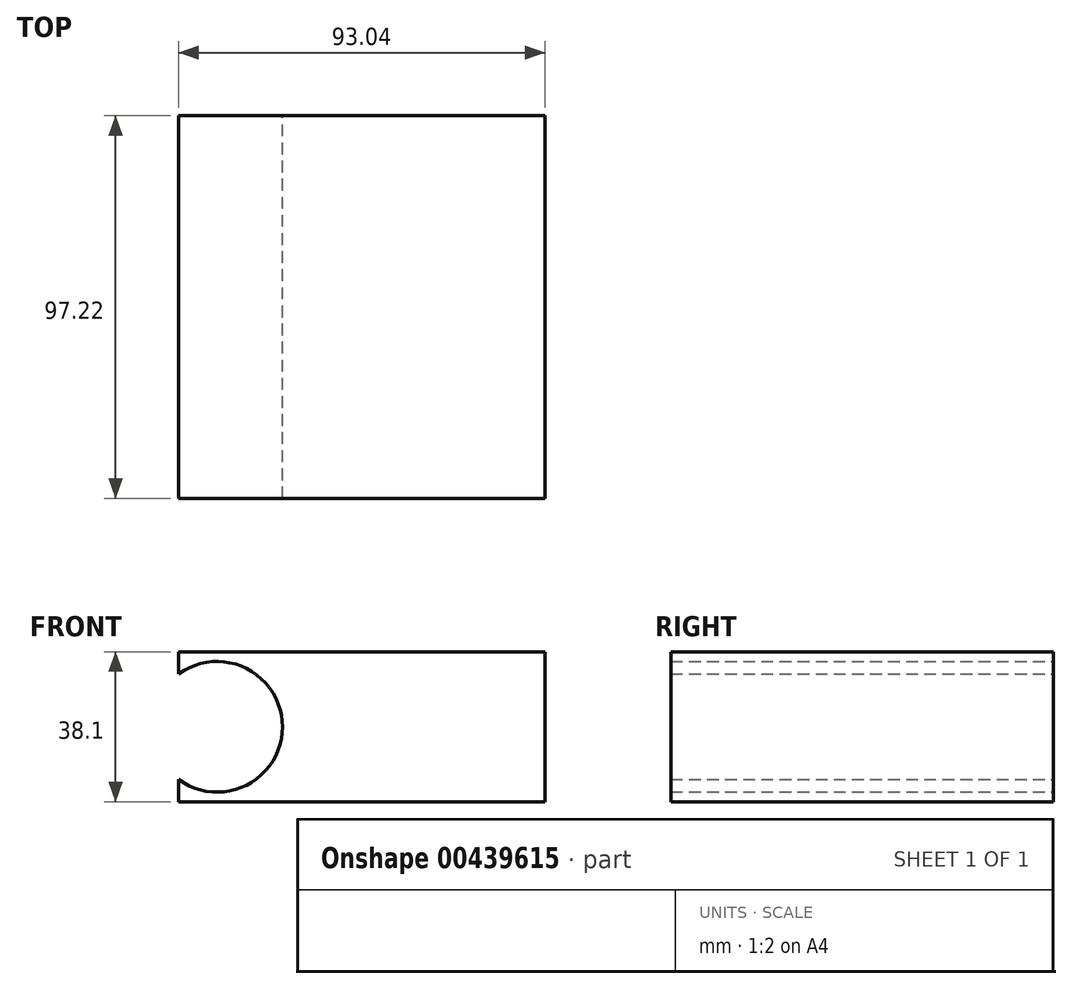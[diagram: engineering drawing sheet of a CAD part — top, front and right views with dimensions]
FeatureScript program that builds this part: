
annotation { "Feature Type Name" : "Feature", "Feature Type Description" : "" }
export const myFeature = defineFeature(function(context is Context, id is Id, definition is map)
    precondition{}
    {
        {
            var Q0;
            Q0=qCreatedBy(makeId("Top.planeOp"),FACE);
            var sketch = newSketch(context, id + "F0", { "sketchPlane" : qUnion([Q0])});
            skLineSegment(sketch, "E0.bottom", {"start": v(46.52, 48.61) * mm, "end": v(-46.52, 48.61) * mm});
            skLineSegment(sketch, "E0.top", {"start": v(46.52, -48.61) * mm, "end": v(-46.52, -48.61) * mm});
            skLineSegment(sketch, "E0.left", {"start": v(46.52, 48.61) * mm, "end": v(46.52, -48.61) * mm});
            skLineSegment(sketch, "E0.right", {"start": v(-46.52, 48.61) * mm, "end": v(-46.52, -48.61) * mm});
            skPoint(sketch, "E0.middle", {"position": v(0, 0) * mm});
            skSolve(sketch);
        }
        {
            var Q0;
            Q0 = qSketchRegion(id + "F0", true);
            extrude(context, id + "F1", {"entities" : qUnion([Q0]), "depth" : 38.1 * mm});
        }
        {
            var Q0;
            Q0=makeQuery(id+"F1.opExtrude","SWEPT_FACE",FACE,{"disambiguationData":[OSD([sQuery(id+"F0.wireOp",EDGE,"E0.bottom")])]});
            var sketch = newSketch(context, id + "F2", { "sketchPlane" : qUnion([Q0])});
            skCircle(sketch, "E1", {"center": v(36.75, 19.05) * mm, "radius": 16.6 * mm});
            skPoint(sketch, "E1.centerSnap0", {"position": v(46.52, 19.05) * mm});
            skSolve(sketch);
        }
        {
            var Q0;
            Q0 = qSketchRegion(id + "F2", true);
            extrude(context, id + "F3", {"entities" : qUnion([Q0]), "operationType" : NewBodyOperationType.REMOVE, "oppositeDirection" : true, "depth" : 134.37 * mm});
        }
    });
